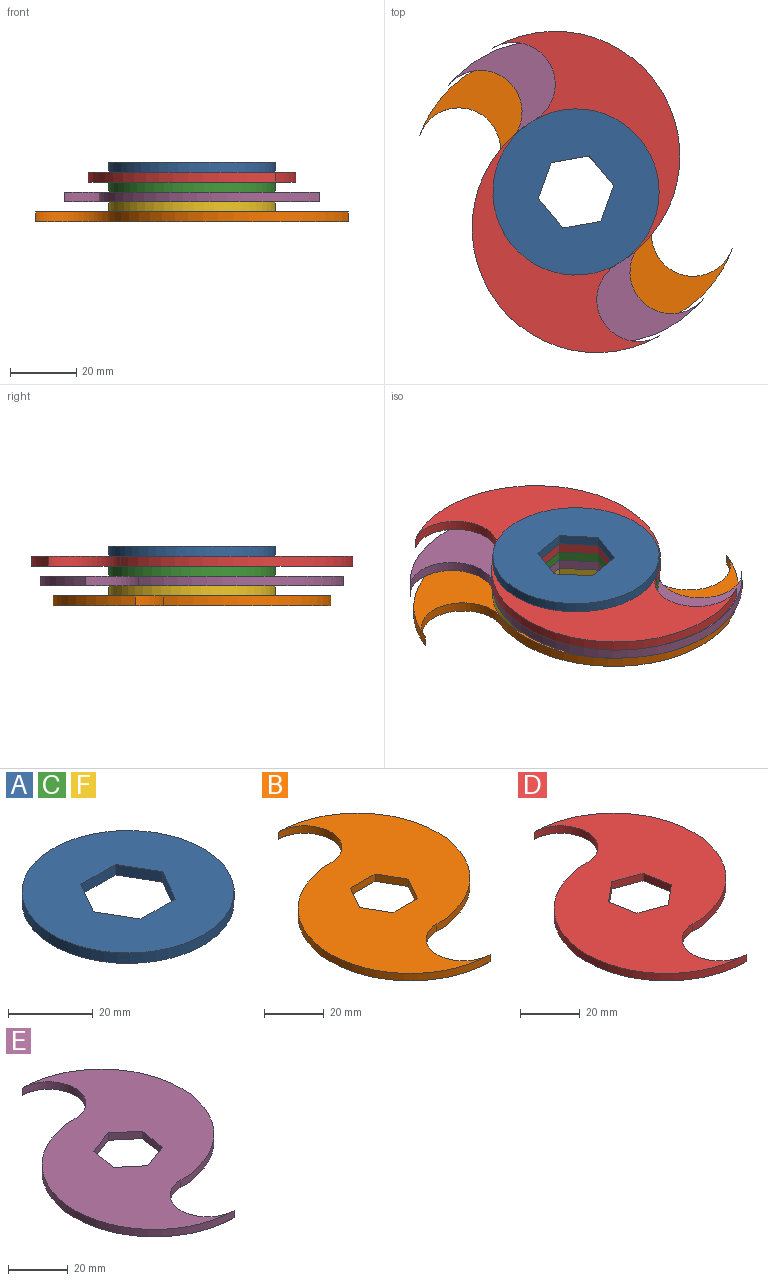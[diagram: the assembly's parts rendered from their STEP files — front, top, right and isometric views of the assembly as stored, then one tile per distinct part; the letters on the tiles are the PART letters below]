
ASSEMBLY  parts=6 mates=5
PART A: 9 faces, bbox 50x50x3 mm
  f0: plane 10x5.77mm, normal (-0.87,0.5,0), area 34.6mm2, adj f1,f5,f7,f8
  f1: plane 11.55x3mm, normal (0,1,0), area 34.6mm2, adj f0,f2,f7,f8
  f2: plane 10x5.77mm, normal (0.87,0.5,0), area 34.6mm2, adj f1,f3,f7,f8
  f3: plane 10x5.77mm, normal (0.87,-0.5,0), area 34.6mm2, adj f2,f4,f7,f8
  f4: plane 11.55x3mm, normal (0,-1,0), area 34.6mm2, adj f3,f5,f7,f8
  f5: plane 10x5.77mm, normal (-0.87,-0.5,0), area 34.6mm2, adj f0,f4,f7,f8
  f6: cylinder r=25mm len=50mm, axis (0,0,-1), area 471.2mm2, adj f7,f8
  f7: plane 50x50mm, normal (0,0,1), area 1617.1mm2, adj f0,f1,f2,f3,f4,f5,f6
  f8: plane 50x50mm, normal (0,0,-1), area 1617.1mm2, adj f0,f1,f2,f3,f4,f5,f6
PART B: 12 faces, bbox 75x100x3 mm
  f0: plane 100x75mm, normal (0,0,1), area 3580.6mm2, adj f1,f2,f3,f4,f6,f7,f8,f9
  f1: cylinder r=12.5mm len=25mm, axis (0,0,-1), area 117.8mm2, adj f0,f2,f4,f5
  f2: cylinder r=37.5mm len=75mm, axis (0,0,-1), area 353.4mm2, adj f0,f1,f3,f5
  f3: cylinder r=12.5mm len=25mm, axis (0,0,-1), area 117.8mm2, adj f0,f2,f4,f5
  f4: cylinder r=37.5mm len=75mm, axis (0,0,-1), area 353.4mm2, adj f0,f1,f3,f5
  f5: plane 100x75mm, normal (0,0,-1), area 3580.6mm2, adj f1,f2,f3,f4,f6,f7,f8,f9
  f6: plane 10x5.77mm, normal (-0.87,-0.5,0), area 34.6mm2, adj f0,f5,f7,f11
  f7: plane 11.55x3mm, normal (0,-1,0), area 34.6mm2, adj f0,f5,f6,f8
  f8: plane 10x5.77mm, normal (0.87,-0.5,0), area 34.6mm2, adj f0,f5,f7,f9
  f9: plane 10x5.77mm, normal (0.87,0.5,0), area 34.6mm2, adj f0,f5,f8,f10
  f10: plane 11.55x3mm, normal (0,1,0), area 34.6mm2, adj f0,f5,f9,f11
  f11: plane 10x5.77mm, normal (-0.87,0.5,0), area 34.6mm2, adj f0,f5,f6,f10
PART C: same geometry as A
PART D: 12 faces, bbox 75x100x3 mm
  f0: plane 100x75mm, normal (0,0,1), area 3580.6mm2, adj f2,f3,f4,f5,f6,f7,f8,f9
  f1: plane 100x75mm, normal (0,0,-1), area 3580.6mm2, adj f2,f3,f4,f5,f6,f7,f8,f9
  f2: cylinder r=12.5mm len=25mm, axis (0,0,-1), area 117.8mm2, adj f0,f1,f3,f5
  f3: cylinder r=37.5mm len=75mm, axis (0,0,-1), area 353.4mm2, adj f0,f1,f2,f4
  f4: cylinder r=12.5mm len=25mm, axis (0,0,-1), area 117.8mm2, adj f0,f1,f3,f5
  f5: cylinder r=37.5mm len=75mm, axis (0,0,-1), area 353.4mm2, adj f0,f1,f2,f4
  f6: plane 11.37x3mm, normal (-0.98,-0.17,0), area 34.6mm2, adj f0,f1,f7,f11
  f7: plane 10.85x3.95mm, normal (-0.34,-0.94,0), area 34.6mm2, adj f0,f1,f6,f8
  f8: plane 8.85x7.42mm, normal (0.64,-0.77,0), area 34.6mm2, adj f0,f1,f7,f9
  f9: plane 11.37x3mm, normal (0.98,0.17,0), area 34.6mm2, adj f0,f1,f8,f10
  f10: plane 10.85x3.95mm, normal (0.34,0.94,0), area 34.6mm2, adj f0,f1,f9,f11
  f11: plane 8.85x7.42mm, normal (-0.64,0.77,0), area 34.6mm2, adj f0,f1,f6,f10
PART E: 12 faces, bbox 75x100x3 mm
  f0: plane 100x75mm, normal (0,0,1), area 3580.6mm2, adj f2,f3,f4,f5,f6,f7,f8,f9
  f1: plane 100x75mm, normal (0,0,-1), area 3580.6mm2, adj f2,f3,f4,f5,f6,f7,f8,f9
  f2: cylinder r=12.5mm len=25mm, axis (0,0,-1), area 117.8mm2, adj f0,f1,f3,f5
  f3: cylinder r=37.5mm len=75mm, axis (0,0,-1), area 353.4mm2, adj f0,f1,f2,f4
  f4: cylinder r=12.5mm len=25mm, axis (0,0,-1), area 117.8mm2, adj f0,f1,f3,f5
  f5: cylinder r=37.5mm len=75mm, axis (0,0,-1), area 353.4mm2, adj f0,f1,f2,f4
  f6: plane 8.85x7.42mm, normal (-0.64,-0.77,0), area 34.6mm2, adj f0,f1,f7,f11
  f7: plane 10.85x3.95mm, normal (0.34,-0.94,0), area 34.6mm2, adj f0,f1,f6,f8
  f8: plane 11.37x3mm, normal (0.98,-0.17,0), area 34.6mm2, adj f0,f1,f7,f9
  f9: plane 8.85x7.42mm, normal (0.64,0.77,0), area 34.6mm2, adj f0,f1,f8,f10
  f10: plane 10.85x3.95mm, normal (-0.34,0.94,0), area 34.6mm2, adj f0,f1,f9,f11
  f11: plane 11.37x3mm, normal (-0.98,0.17,0), area 34.6mm2, adj f0,f1,f6,f10
PART F: same geometry as A
PLACE A rot(axis=(0.82,0.57,0),180deg) t=(0.63,2.78,-30.19)mm
PLACE B rot(axis=(0,0,1),70deg) t=(0.63,2.78,-48.19)mm
PLACE C rot(axis=(0,0,1),10deg) t=(0.63,2.78,-39.19)mm
PLACE D rot(axis=(0,0,1),30deg) t=(0.63,2.78,-39.19)mm
PLACE E rot(axis=(0,0,1),50deg) t=(0.63,2.78,-48.19)mm
PLACE F rot(axis=(0,0,1),10deg) t=(0.63,2.78,-45.19)mm
MATE fastened F.f2 <-> E.f8  axis (0.77,0.64,0) through (-7.03,-3.64,-42.19)mm
MATE fastened C.f2 <-> D.f9  axis (0.77,0.64,0) through (-7.03,-3.64,-36.19)mm
MATE fastened D.f8 <-> E.f7  axis (0.94,-0.34,0) through (-8.76,6.2,-36.19)mm
MATE fastened A.f2 <-> D.f9  axis (0.77,0.64,0) through (-7.03,-3.64,-33.19)mm
MATE fastened E.f7 <-> B.f7  axis (0.94,-0.34,0) through (-8.76,6.2,-42.19)mm
